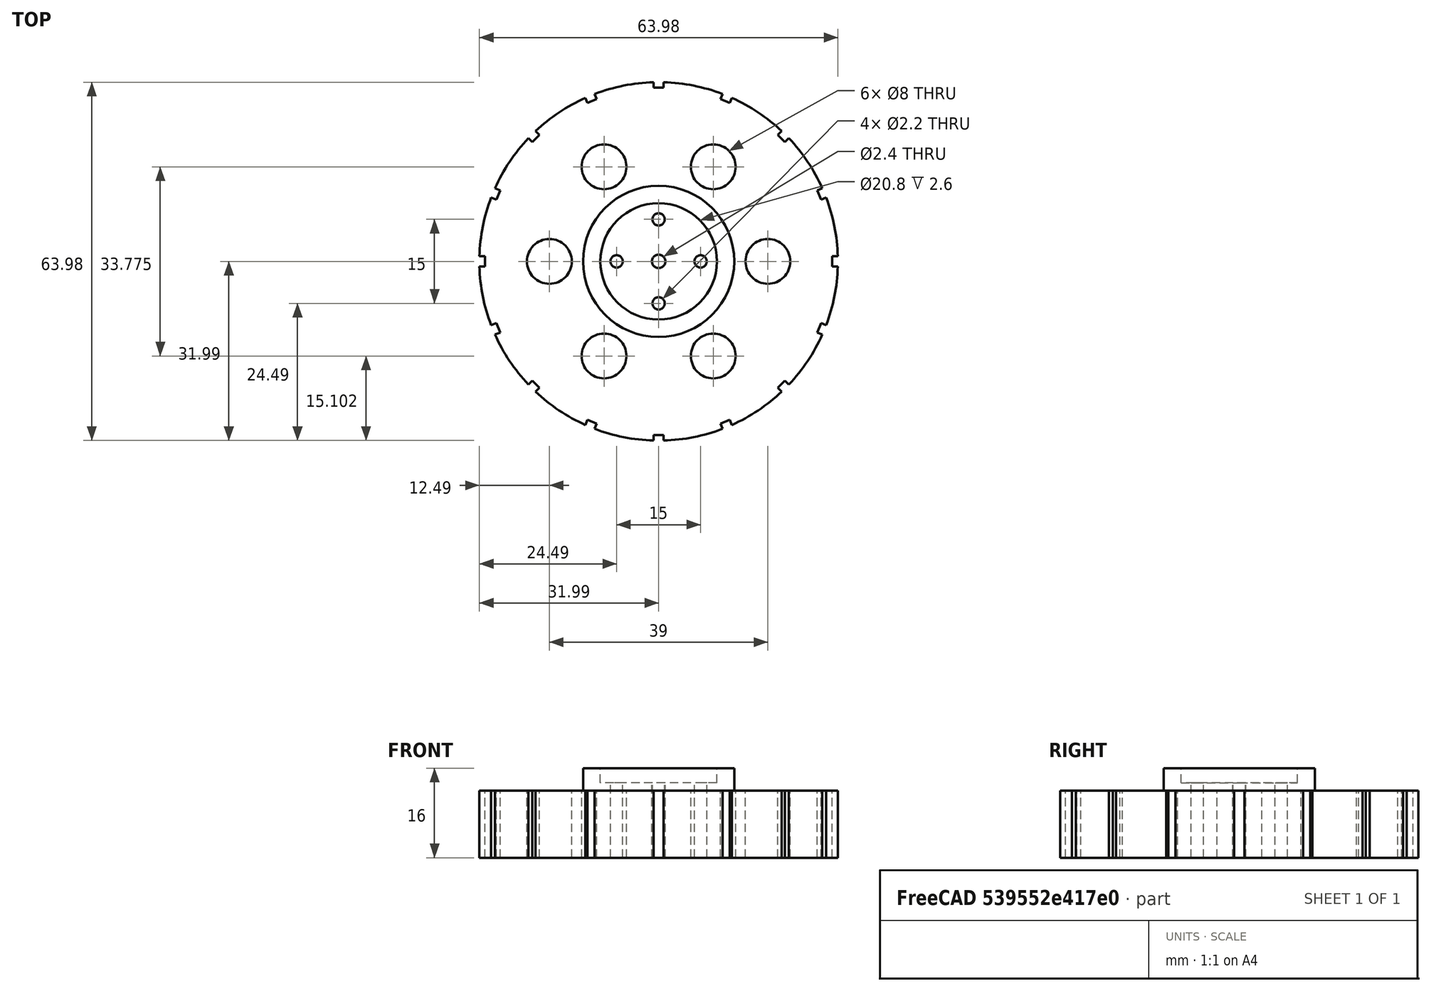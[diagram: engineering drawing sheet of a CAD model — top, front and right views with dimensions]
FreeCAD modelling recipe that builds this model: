
FCSTD DOCUMENT  (FreeCAD 1.2R20251230 (Git shallow))
Label: servo_wheel_360_history
License: Creative Commons Attribution 4.0
LicenseURL: https://creativecommons.org/licenses/by/4.0/
objects: Part::Feature×7, Part::Cut×5, Part::Fuse×1
note: 13 computed .brp shape members not serialized (recipe doc carries the construction recipe); baked Part::Feature solids carry a one-line shape summary decoded from their .brp

FEATURE [Part::Feature] _01_WheelBody_Cylinder
  shape: bbox 64 x 64 x 12 mm, 3 faces (baked)
FEATURE [Part::Feature] _02_FrontHub_Cylinder
  shape: bbox 27 x 27 x 4 mm, 3 faces (baked)
FEATURE [Part::Fuse] _03_Fuse_WheelBody_FrontHub
  Base = -> _01_WheelBody_Cylinder
  Refine = true
  Tool = -> _02_FrontHub_Cylinder
FEATURE [Part::Feature] _04_Tool_CenterScrewHole
  shape: bbox 2.4 x 2.4 x 18 mm, 3 faces (baked)
FEATURE [Part::Cut] _05_Cut_CenterScrewHole
  Base = -> _03_Fuse_WheelBody_FrontHub
  Refine = true
  Tool = -> _04_Tool_CenterScrewHole
FEATURE [Part::Feature] _06_Tool_ServoHornPocket
  shape: bbox 20.8 x 20.8 x 3.6 mm, 3 faces (baked)
FEATURE [Part::Cut] _07_Cut_ServoHornPocket
  Base = -> _05_Cut_CenterScrewHole
  Refine = true
  Tool = -> _06_Tool_ServoHornPocket
FEATURE [Part::Feature] _08_Tool_HornScrewHoles_4x
  shape: bbox 17.2 x 17.2 x 18 mm, 12 faces, 4 solids (baked)
FEATURE [Part::Cut] _09_Cut_HornScrewHoles
  Base = -> _07_Cut_ServoHornPocket
  Refine = true
  Tool = -> _08_Tool_HornScrewHoles_4x
FEATURE [Part::Feature] _10_Tool_SpokeCutouts_6x
  shape: bbox 47 x 41.77 x 18 mm, 18 faces, 6 solids (baked)
FEATURE [Part::Cut] _11_Cut_SpokeCutouts
  Base = -> _09_Cut_HornScrewHoles
  Refine = true
  Tool = -> _10_Tool_SpokeCutouts_6x
FEATURE [Part::Feature] _12_Tool_RimGripGrooves_16x
  shape: bbox 68 x 68 x 14 mm, 96 faces, 16 solids (baked)
FEATURE [Part::Cut] _13_Final_ServoWheel360
  Base = -> _11_Cut_SpokeCutouts
  Refine = true
  Tool = -> _12_Tool_RimGripGrooves_16x
